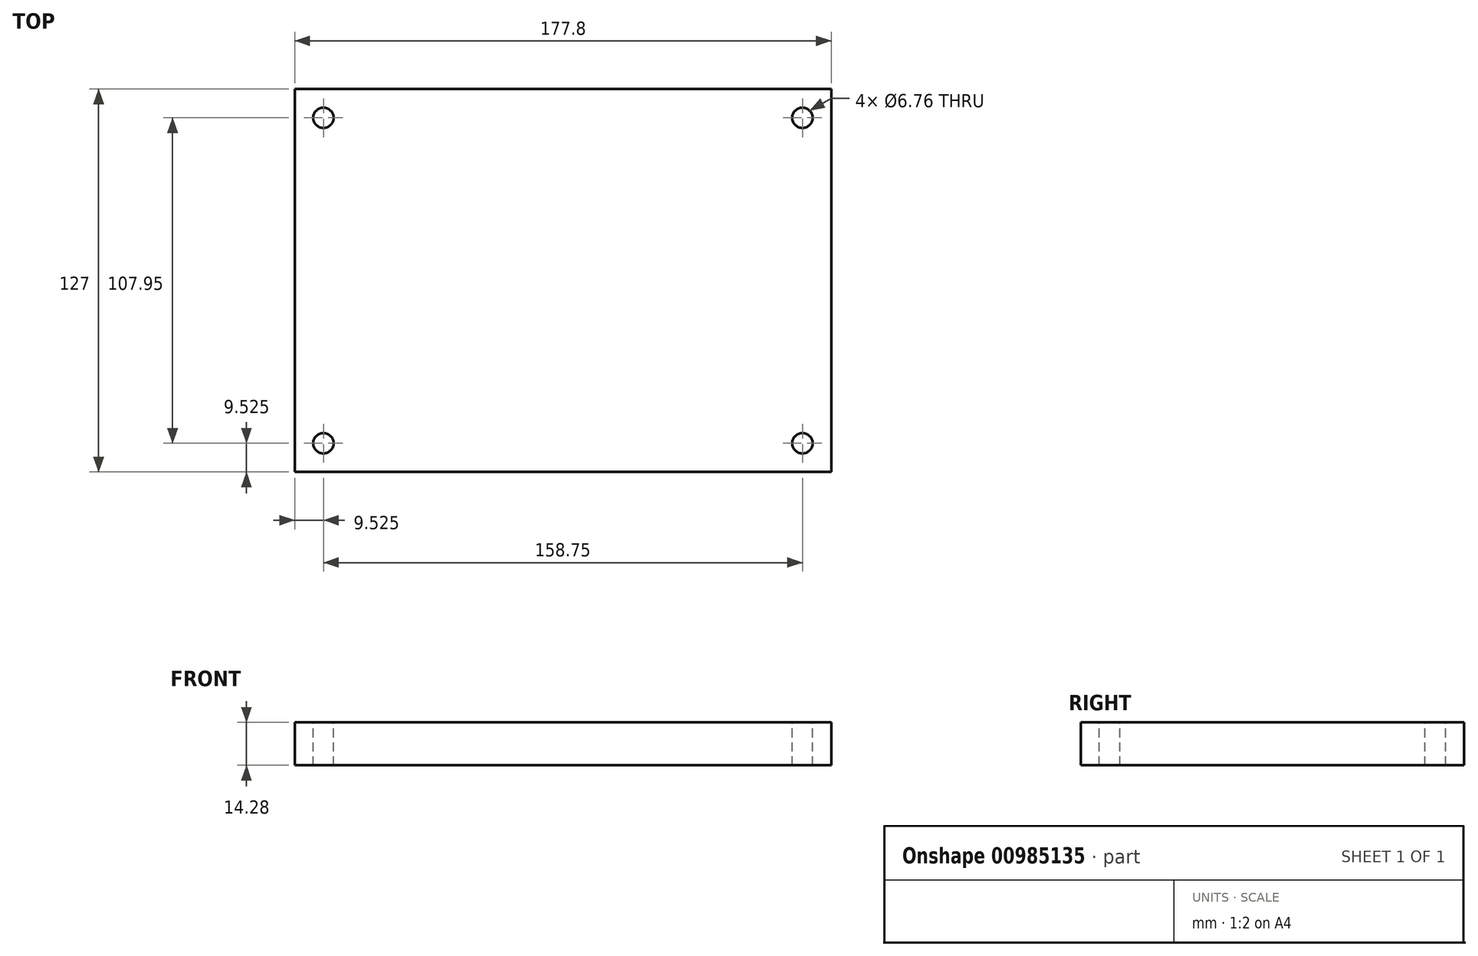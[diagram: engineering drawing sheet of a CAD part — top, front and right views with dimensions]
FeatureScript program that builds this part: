
annotation { "Feature Type Name" : "Feature", "Feature Type Description" : "" }
export const myFeature = defineFeature(function(context is Context, id is Id, definition is map)
    precondition{}
    {
        {
            var Q0;
            Q0=qCreatedBy(makeId("Top.planeOp"),FACE);
            var sketch = newSketch(context, id + "F0", { "sketchPlane" : qUnion([Q0])});
            skLineSegment(sketch, "E0.bottom", {"start": v(88.9, -63.5) * mm, "end": v(-88.9, -63.5) * mm});
            skLineSegment(sketch, "E0.top", {"start": v(88.9, 63.5) * mm, "end": v(-88.9, 63.5) * mm});
            skLineSegment(sketch, "E0.left", {"start": v(88.9, -63.5) * mm, "end": v(88.9, 63.5) * mm});
            skLineSegment(sketch, "E0.right", {"start": v(-88.9, -63.5) * mm, "end": v(-88.9, 63.5) * mm});
            skPoint(sketch, "E0.middle", {"position": v(0, 0) * mm});
            skCircle(sketch, "E1", {"center": v(79.38, 53.97) * mm, "radius": 3.38 * mm});
            skCircle(sketch, "E2", {"center": v(79.38, -53.98) * mm, "radius": 3.38 * mm});
            skCircle(sketch, "E3", {"center": v(-79.38, 53.97) * mm, "radius": 3.38 * mm});
            skCircle(sketch, "E4", {"center": v(-79.37, -53.98) * mm, "radius": 3.38 * mm});
            skSolve(sketch);
        }
        {
            var Q0;
            Q0=makeQuery(id+"F0.imprint","IMPRINT",FACE,{"disambiguationData":[TD([[makeQuery(id+"F0.imprint","IMPRINT",EDGE,{"derivedFrom":sQuery(id+"F0.wireOp",EDGE,"E0.bottom")}),-1.0]])]});
            extrude(context, id + "F1", {"entities" : qUnion([Q0]), "endBound" : BoundingType.SYMMETRIC, "oppositeDirection" : true, "depth" : 14.29 * mm, "offsetDistance" : 25.4 * mm});
        }
    });
